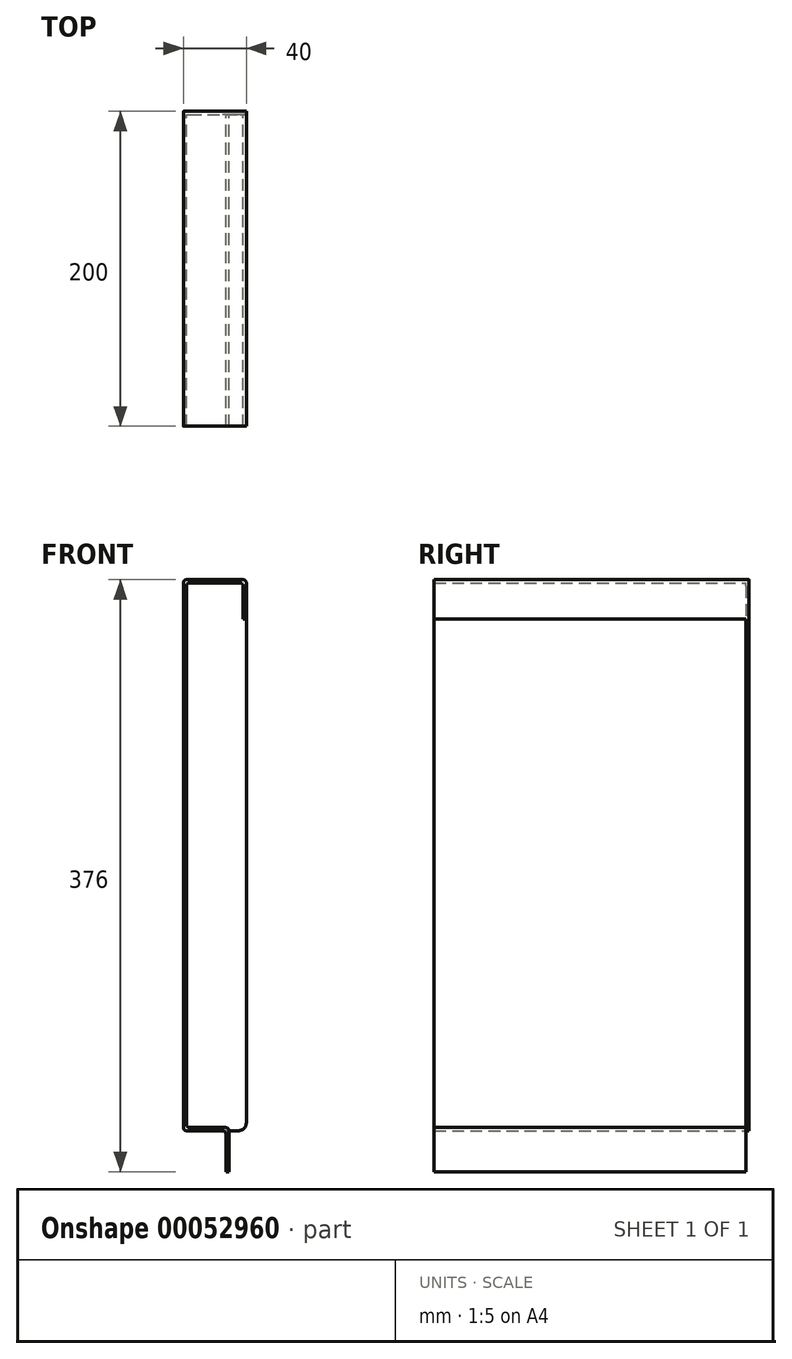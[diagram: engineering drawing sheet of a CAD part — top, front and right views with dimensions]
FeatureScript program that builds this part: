
annotation { "Feature Type Name" : "Feature", "Feature Type Description" : "" }
export const myFeature = defineFeature(function(context is Context, id is Id, definition is map)
    precondition{}
    {
        {
            var Q0;
            Q0=qCreatedBy(makeId("Front.planeOp"),FACE);
            var sketch = newSketch(context, id + "F0", { "sketchPlane" : qUnion([Q0])});
            skLineSegment(sketch, "E0", {"start": v(0, 0) * mm, "end": v(0, -350) * mm});
            skLineSegment(sketch, "E1", {"start": v(0, -350) * mm, "end": v(27, -350) * mm});
            skLineSegment(sketch, "E2", {"start": v(27, -350) * mm, "end": v(27, -376) * mm});
            skLineSegment(sketch, "E3", {"start": v(0, 0) * mm, "end": v(40, 0) * mm});
            skLineSegment(sketch, "E4", {"start": v(40, 0) * mm, "end": v(40, -25) * mm});
            skLineSegment(sketch, "E5.0", {"start": v(38, -2) * mm, "end": v(38, -25) * mm});
            skLineSegment(sketch, "E5.1", {"start": v(29, -348) * mm, "end": v(29, -376) * mm});
            skLineSegment(sketch, "E5.2", {"start": v(2, -348) * mm, "end": v(29, -348) * mm});
            skLineSegment(sketch, "E5.3", {"start": v(2, -2) * mm, "end": v(2, -348) * mm});
            skLineSegment(sketch, "E5.4", {"start": v(2, -2) * mm, "end": v(38, -2) * mm});
            skLineSegment(sketch, "E6", {"start": v(38, -25) * mm, "end": v(40, -25) * mm});
            skLineSegment(sketch, "E7", {"start": v(27, -376) * mm, "end": v(29, -376) * mm});
            skSolve(sketch);
        }
        {
            var Q0;
            Q0=qCreatedBy(makeId("Top.planeOp"),FACE);
            var sketch = newSketch(context, id + "F1", { "sketchPlane" : qUnion([Q0])});
            skLineSegment(sketch, "E8", {"start": v(0, 0) * mm, "end": v(0, 198) * mm});
            skSolve(sketch);
        }
        {
            var Q0;
            Q0=qSketchRegion(id+"F0",true);
            var Q1;
            Q1=qConstructionFilter(qBodyType(qCreatedBy(id+"F1",EDGE),BodyType.WIRE),ConstructionObject.NO);
            sweep(context, id + "F2", {"profiles" : qUnion([Q0]), "path" : qUnion([Q1])});
        }
        {
            var Q0;
            Q0=makeQuery(id+"F2.opSweep","CAP_FACE",FACE,{"disambiguationData":[OSD([sQuery(id+"F0.wireOp",EDGE,"E0"),sQuery(id+"F0.wireOp",EDGE,"E1"),sQuery(id+"F0.wireOp",EDGE,"E2"),sQuery(id+"F0.wireOp",EDGE,"E3"),sQuery(id+"F0.wireOp",EDGE,"E4"),sQuery(id+"F0.wireOp",EDGE,"E5.0"),sQuery(id+"F0.wireOp",EDGE,"E5.1"),sQuery(id+"F0.wireOp",EDGE,"E5.2"),sQuery(id+"F0.wireOp",EDGE,"E5.3"),sQuery(id+"F0.wireOp",EDGE,"E5.4"),sQuery(id+"F0.wireOp",EDGE,"E6"),sQuery(id+"F0.wireOp",EDGE,"E7"),sQuery(id+"F1.wireOp",VERTEX,"E8.end")])],"isStart":false});
            var sketch = newSketch(context, id + "F3", { "sketchPlane" : qUnion([Q0])});
            skLineSegment(sketch, "E9.0", {"start": v(0, -350) * mm, "end": v(0, 0) * mm});
            skLineSegment(sketch, "E10.0", {"start": v(-40, 0) * mm, "end": v(0, 0) * mm});
            skLineSegment(sketch, "E11.0", {"start": v(-40, -25) * mm, "end": v(-40, 0) * mm});
            skLineSegment(sketch, "E12.0", {"start": v(-40, -25) * mm, "end": v(-40, -345) * mm});
            skArc(sketch, "E13.0", {"start": v(-35, -350) * mm, "mid": v(-38.54, -348.54) * mm, "end": v(-40, -345) * mm});
            skLineSegment(sketch, "E14.0", {"start": v(-35, -350) * mm, "end": v(-29, -350) * mm});
            skLineSegment(sketch, "E15.0", {"start": v(-27, -350) * mm, "end": v(0, -350) * mm});
            skLineSegment(sketch, "E16", {"start": v(-29, -350) * mm, "end": v(-27, -350) * mm});
            skSolve(sketch);
        }
        {
            var Q0;
            Q0=qSketchRegion(id+"F3",true);
            extrude(context, id + "F4", {"entities" : qUnion([Q0]), "operationType" : NewBodyOperationType.ADD, "depth" : 2 * mm});
        }
        {
            var Q0;
            Q0=makeQuery(id+"F4.boolean.opBoolean","MERGE",EDGE,{"derivedFrom":[makeQuery(id+"F2.opSweep","SWEPT_EDGE",EDGE,{"disambiguationData":[OSD([sQuery(id+"F0.wireOp",EDGE,"E3"),sQuery(id+"F0.wireOp",EDGE,"E4"),sQuery(id+"F1.wireOp",EDGE,"E8")])]}),makeQuery(id+"F4.opExtrude","SWEPT_EDGE",EDGE,{"disambiguationData":[OSD([sQuery(id+"F3.wireOp",EDGE,"E10.0"),sQuery(id+"F3.wireOp",EDGE,"E11.0")])]})]});
            var Q1;
            Q1=makeQuery(id+"F4.boolean.opBoolean","MERGE",EDGE,{"derivedFrom":[makeQuery(id+"F2.opSweep","SWEPT_EDGE",EDGE,{"disambiguationData":[OSD([sQuery(id+"F0.wireOp",EDGE,"E0"),sQuery(id+"F0.wireOp",EDGE,"E3"),sQuery(id+"F1.wireOp",EDGE,"E8")])]}),makeQuery(id+"F4.opExtrude","SWEPT_EDGE",EDGE,{"disambiguationData":[OSD([sQuery(id+"F3.wireOp",EDGE,"E9.0"),sQuery(id+"F3.wireOp",EDGE,"E10.0")])]})]});
            var Q2;
            Q2=makeQuery(id+"F2.opSweep","SWEPT_EDGE",EDGE,{"disambiguationData":[OSD([sQuery(id+"F0.wireOp",EDGE,"E5.2"),sQuery(id+"F0.wireOp",EDGE,"E5.3"),sQuery(id+"F1.wireOp",EDGE,"E8")])]});
            var Q3;
            Q3=makeQuery(id+"F2.opSweep","SWEPT_EDGE",EDGE,{"disambiguationData":[OSD([sQuery(id+"F0.wireOp",EDGE,"E5.1"),sQuery(id+"F0.wireOp",EDGE,"E5.2"),sQuery(id+"F1.wireOp",EDGE,"E8")])]});
            var Q4;
            Q4=makeQuery(id+"F2.opSweep","SWEPT_EDGE",EDGE,{"disambiguationData":[OSD([sQuery(id+"F0.wireOp",EDGE,"E1"),sQuery(id+"F0.wireOp",EDGE,"E2"),sQuery(id+"F1.wireOp",EDGE,"E8")])]});
            var Q5;
            Q5=makeQuery(id+"F4.boolean.opBoolean","MERGE",EDGE,{"derivedFrom":[makeQuery(id+"F2.opSweep","SWEPT_EDGE",EDGE,{"disambiguationData":[OSD([sQuery(id+"F0.wireOp",EDGE,"E0"),sQuery(id+"F0.wireOp",EDGE,"E1"),sQuery(id+"F1.wireOp",EDGE,"E8")])]}),makeQuery(id+"F4.opExtrude","SWEPT_EDGE",EDGE,{"disambiguationData":[OSD([sQuery(id+"F3.wireOp",EDGE,"E9.0"),sQuery(id+"F3.wireOp",EDGE,"E15.0")])]})]});
            var Q6;
            Q6=makeQuery(id+"F2.opSweep","SWEPT_EDGE",EDGE,{"disambiguationData":[OSD([sQuery(id+"F0.wireOp",EDGE,"E5.0"),sQuery(id+"F0.wireOp",EDGE,"E5.4"),sQuery(id+"F1.wireOp",EDGE,"E8")])]});
            var Q7;
            Q7=makeQuery(id+"F2.opSweep","SWEPT_EDGE",EDGE,{"disambiguationData":[OSD([sQuery(id+"F0.wireOp",EDGE,"E5.3"),sQuery(id+"F0.wireOp",EDGE,"E5.4"),sQuery(id+"F1.wireOp",EDGE,"E8")])]});
            fillet(context, id + "F5", {"entities" : qUnion([Q0, Q1, Q2, Q3, Q4, Q5, Q6, Q7]), "radius" : 2 * mm, "tangentPropagation" : true, "allowEdgeOverflow" : false});
        }
    });
